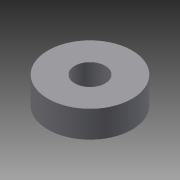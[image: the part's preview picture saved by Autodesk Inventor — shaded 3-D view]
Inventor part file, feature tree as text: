
AUTODESK INVENTOR PART (.ipt)
format: ipt  version: 2015 SP1 (Build 190203100, 203)  size: 73,728 bytes
history: native  units: mm
features: extrude x1, sketch x1
ambient origin geometry x8: Origin, YZ Plane, XZ Plane, XY Plane, X Axis, Y Axis, Z Axis, Center Point
bodies: Solid1 (feature_tree)
feature tree (2):
  extrude  "Extrusion1"  Depth=7.0mm
  sketch  "Sketch1"  dims[d0=8.0mm d1=22.0mm d2=7.0mm d3=0.0mm]
